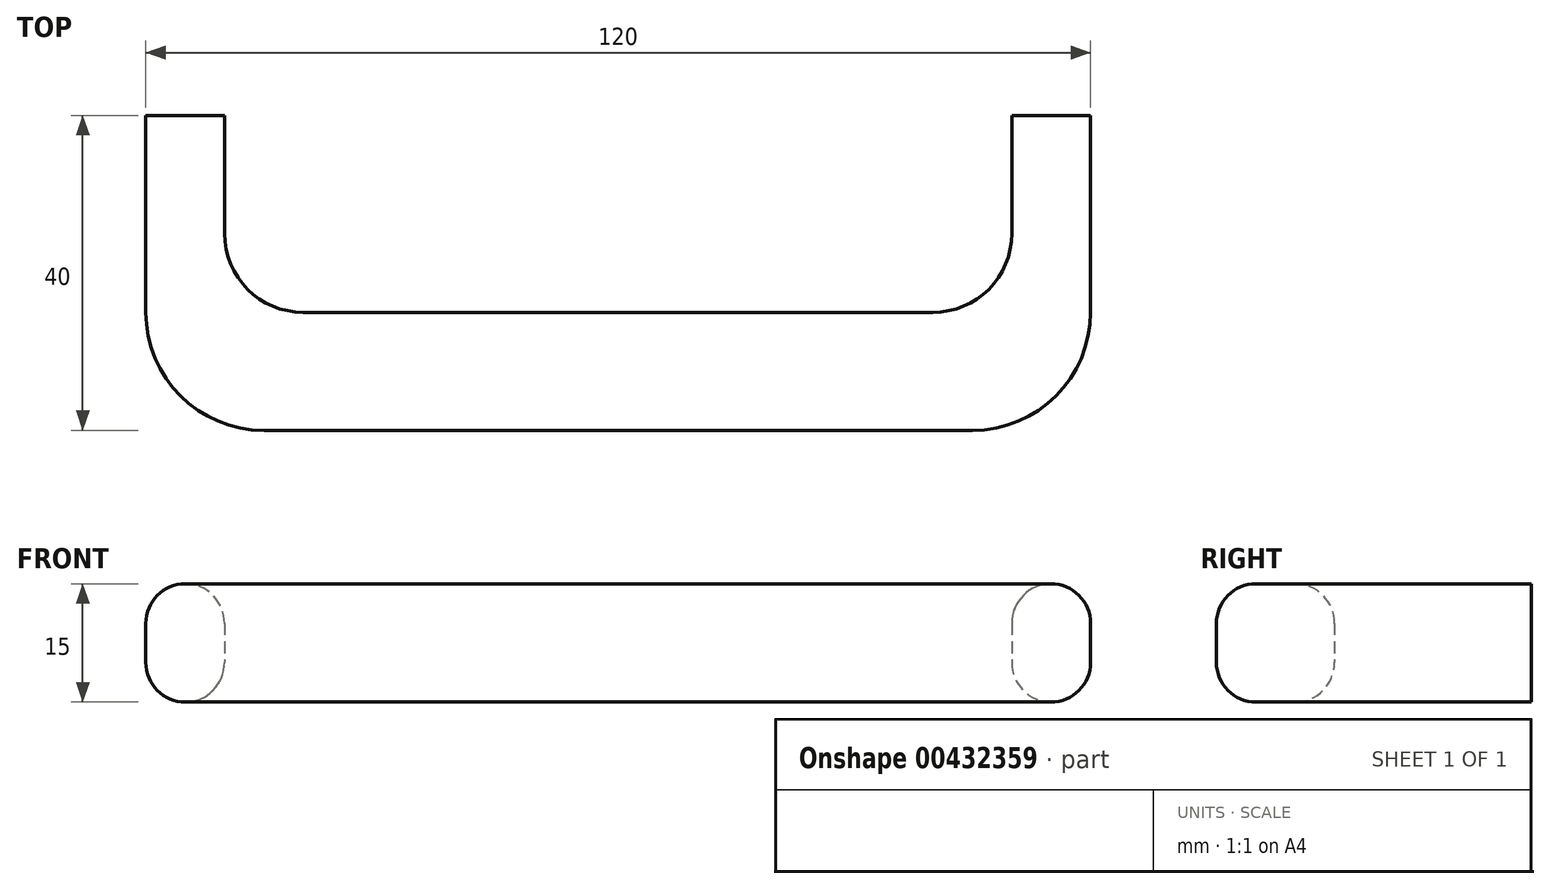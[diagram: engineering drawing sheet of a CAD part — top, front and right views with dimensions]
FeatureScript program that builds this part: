
annotation { "Feature Type Name" : "Feature", "Feature Type Description" : "" }
export const myFeature = defineFeature(function(context is Context, id is Id, definition is map)
    precondition{}
    {
        {
            var Q0;
            Q0=qCreatedBy(makeId("Top.planeOp"),FACE);
            var sketch = newSketch(context, id + "F0", { "sketchPlane" : qUnion([Q0])});
            skLineSegment(sketch, "E0", {"start": v(-53.4, 0.17) * mm, "end": v(36.6, 0.17) * mm});
            skLineSegment(sketch, "E1", {"start": v(51.6, 15.17) * mm, "end": v(51.6, 40.17) * mm});
            skLineSegment(sketch, "E2", {"start": v(-68.4, 15.17) * mm, "end": v(-68.4, 40.17) * mm});
            skArc(sketch, "E3.filletArc", {"start": v(-68.4, 15.17) * mm, "mid": v(-64.01, 4.56) * mm, "end": v(-53.4, 0.17) * mm});
            skArc(sketch, "E4.filletArc", {"start": v(36.6, 0.17) * mm, "mid": v(47.2, 4.56) * mm, "end": v(51.6, 15.17) * mm});
            skLineSegment(sketch, "E5", {"start": v(-68.4, 40.17) * mm, "end": v(-58.4, 40.17) * mm});
            skLineSegment(sketch, "E6", {"start": v(-58.4, 40.17) * mm, "end": v(-58.4, 25.17) * mm});
            skLineSegment(sketch, "E7", {"start": v(-48.4, 15.17) * mm, "end": v(31.6, 15.17) * mm});
            skLineSegment(sketch, "E8", {"start": v(41.6, 25.17) * mm, "end": v(41.6, 40.17) * mm});
            skLineSegment(sketch, "E9", {"start": v(41.6, 40.17) * mm, "end": v(51.6, 40.17) * mm});
            skArc(sketch, "E10.filletArc", {"start": v(31.6, 15.17) * mm, "mid": v(38.66, 18.1) * mm, "end": v(41.6, 25.17) * mm});
            skArc(sketch, "E11.filletArc", {"start": v(-58.4, 25.17) * mm, "mid": v(-55.48, 18.1) * mm, "end": v(-48.4, 15.17) * mm});
            skSolve(sketch);
        }
        {
            var Q0;
            Q0 = qSketchRegion(id + "F0", true);
            extrude(context, id + "F1", {"entities" : qUnion([Q0]), "endBound" : BoundingType.SYMMETRIC, "depth" : 15 * mm});
        }
        {
            var Q0;
            Q0=makeQuery(id+"F1.opExtrude","CAP_EDGE",EDGE,{"disambiguationData":[OSD([sQuery(id+"F0.wireOp",EDGE,"E7")])],"isStart":false});
            var Q1;
            Q1=makeQuery(id+"F1.opExtrude","CAP_EDGE",EDGE,{"disambiguationData":[OSD([sQuery(id+"F0.wireOp",EDGE,"E0")])],"isStart":false});
            var Q2;
            Q2=makeQuery(id+"F1.opExtrude","CAP_EDGE",EDGE,{"disambiguationData":[OSD([sQuery(id+"F0.wireOp",EDGE,"E0")])],"isStart":true});
            var Q3;
            Q3=makeQuery(id+"F1.opExtrude","CAP_EDGE",EDGE,{"disambiguationData":[OSD([sQuery(id+"F0.wireOp",EDGE,"E7")])],"isStart":true});
            fillet(context, id + "F2", {"entities" : qUnion([Q0, Q1, Q2, Q3]), "radius" : 5 * mm, "tangentPropagation" : true, "allowEdgeOverflow" : false});
        }
    });
